# Revit family: Drain_Linear-Whitehall-BestCare-WHLD_Series
name_source: partatom
category: Plumbing Fixtures
units: mm (PartAtom-declared; Revit-internal decimal feet)

## family parameters
Cut with Voids When Loaded = No
Host = Face
OmniClass Number = 23.70.50.21.24
OmniClass Title = Waste Water Drains
Part Type = Normal
Room Calculation Point = No
Round Connector Dimension = Use Diameter
Shared = Yes

## types (6) — shared parameters
-F Flashing Flange = Yes
Assembly Code = D2030300
CW Connection = No
Connection Size = 2"
Default Elevation = 0"
Depth = 1 1/2"
Description = BestCare® Ligature-Resistant Linear Drain with Flashing Flange
Finish = Stainless Steel-Whitehall-#4 Satin
HW Connection = No
Installation Type = Floor Mounted
Manufacturer = Whitehall Manufacturing
Material = Stainless Steel-Whitehall-#4 Satin
Product Documentation Link = https://www.whitehallmfg.com
Product Page URL = https://www.whitehallmfg.com
Revised Date = 06/27/2023
URL = https://www.whitehallmfg.com
Vent Connection = No
Waste Connection = Yes
Width = 5 1/4"
zero-valued in all types: CWFU, HWFU, WFU

## per-type parameters (varying)
| type | Extention | Length |
| WHLD-12-F | 6" | 12" |
| WHLD-24-F | 12" | 24" |
| WHLD-36-F | 18" | 36" |
| WHLD-48-F | 24" | 48" |
| WHLD-60-F | 30" | 60" |
| WHLD-30-F | 15" | 30" |

note: column(s) folded — value = type name in every type: Model

## geometry (parser evidence)
native form markers: Sweep x3
no freeform markers — native parametric forms only
